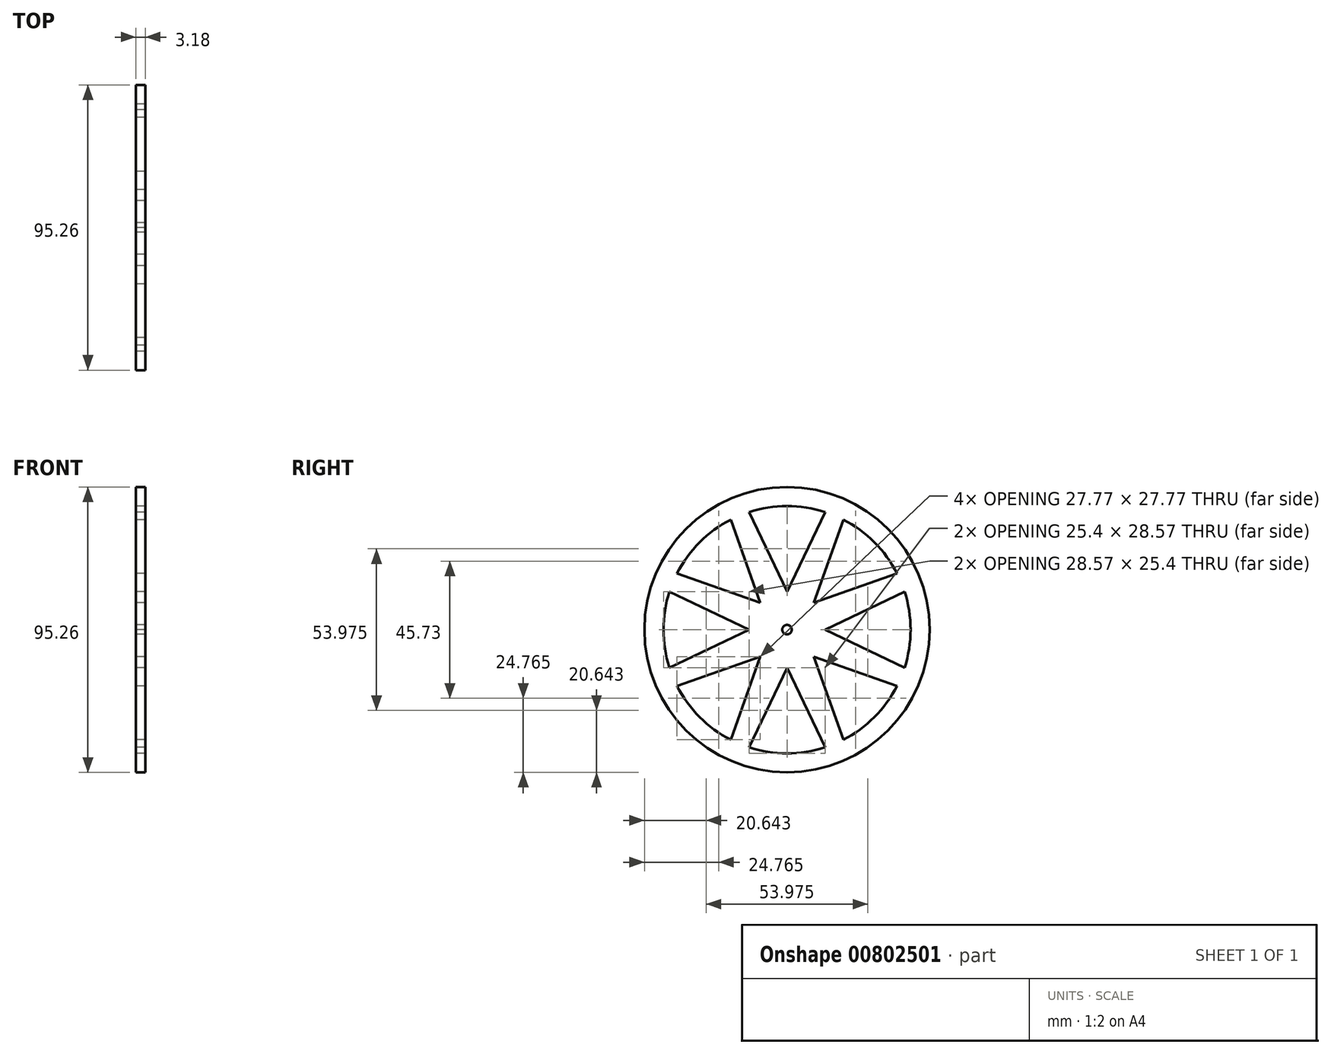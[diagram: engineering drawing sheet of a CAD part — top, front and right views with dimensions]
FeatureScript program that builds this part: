
annotation { "Feature Type Name" : "Feature", "Feature Type Description" : "" }
export const myFeature = defineFeature(function(context is Context, id is Id, definition is map)
    precondition{}
    {
        {
            var Q0;
            Q0=qCreatedBy(makeId("Right.planeOp"),FACE);
            var sketch = newSketch(context, id + "F0", { "sketchPlane" : qUnion([Q0])});
            skCircle(sketch, "E0", {"center": v(0, 0) * mm, "radius": 47.63 * mm});
            skCircle(sketch, "E1", {"center": v(0, 0) * mm, "radius": 41.28 * mm, "construction": true});
            skCircle(sketch, "E2", {"center": v(0, 0) * mm, "radius": 12.7 * mm, "construction": true});
            skArc(sketch, "E3", {"start": v(-12.7, 39.27) * mm, "mid": v(0, 41.28) * mm, "end": v(12.7, 39.27) * mm});
            skLineSegment(sketch, "E4", {"start": v(-12.7, 39.27) * mm, "end": v(0, 12.7) * mm});
            skLineSegment(sketch, "E5", {"start": v(0, 12.7) * mm, "end": v(12.7, 39.27) * mm});
            skLineSegment(sketch, "E6", {"start": v(-80.26, -80.26) * mm, "end": v(80.26, 80.26) * mm, "construction": true});
            skLineSegment(sketch, "E7", {"start": v(93.24, -93.24) * mm, "end": v(-93.24, 93.24) * mm, "construction": true});
            skLineSegment(sketch, "E8", {"start": v(18.79, 36.75) * mm, "end": v(8.98, 8.98) * mm});
            skLineSegment(sketch, "E9", {"start": v(36.75, 18.79) * mm, "end": v(8.98, 8.98) * mm});
            skArc(sketch, "E10", {"start": v(18.79, 36.75) * mm, "mid": v(29.19, 29.19) * mm, "end": v(36.75, 18.79) * mm});
            skArc(sketch, "E11", {"start": v(39.27, 12.7) * mm, "mid": v(41.28, 0) * mm, "end": v(39.27, -12.7) * mm});
            skLineSegment(sketch, "E12", {"start": v(39.27, 12.7) * mm, "end": v(12.7, 0) * mm});
            skLineSegment(sketch, "E13", {"start": v(12.7, 0) * mm, "end": v(39.27, -12.7) * mm});
            skArc(sketch, "E14", {"start": v(36.75, -18.79) * mm, "mid": v(29.19, -29.19) * mm, "end": v(18.79, -36.75) * mm});
            skLineSegment(sketch, "E15", {"start": v(36.75, -18.79) * mm, "end": v(8.98, -8.98) * mm});
            skLineSegment(sketch, "E16", {"start": v(8.98, -8.98) * mm, "end": v(18.79, -36.75) * mm});
            skArc(sketch, "E17", {"start": v(12.7, -39.27) * mm, "mid": v(0, -41.28) * mm, "end": v(-12.7, -39.27) * mm});
            skArc(sketch, "E18", {"start": v(-18.79, -36.75) * mm, "mid": v(-29.19, -29.19) * mm, "end": v(-36.75, -18.79) * mm});
            skArc(sketch, "E19", {"start": v(-39.27, -12.7) * mm, "mid": v(-41.28, 0) * mm, "end": v(-39.27, 12.7) * mm});
            skArc(sketch, "E20", {"start": v(-36.75, 18.79) * mm, "mid": v(-29.19, 29.19) * mm, "end": v(-18.79, 36.75) * mm});
            skLineSegment(sketch, "E21", {"start": v(12.7, -39.27) * mm, "end": v(0, -12.7) * mm});
            skLineSegment(sketch, "E22", {"start": v(0, -12.7) * mm, "end": v(-12.7, -39.27) * mm});
            skLineSegment(sketch, "E23", {"start": v(-18.79, -36.75) * mm, "end": v(-8.98, -8.98) * mm});
            skLineSegment(sketch, "E24", {"start": v(-8.98, -8.98) * mm, "end": v(-36.75, -18.79) * mm});
            skLineSegment(sketch, "E25", {"start": v(-39.27, -12.7) * mm, "end": v(-12.7, 0) * mm});
            skLineSegment(sketch, "E26", {"start": v(-12.7, 0) * mm, "end": v(-39.27, 12.7) * mm});
            skLineSegment(sketch, "E27", {"start": v(-36.75, 18.79) * mm, "end": v(-8.98, 8.98) * mm});
            skLineSegment(sketch, "E28", {"start": v(-8.98, 8.98) * mm, "end": v(-18.79, 36.75) * mm});
            skCircle(sketch, "E29", {"center": v(0, 0) * mm, "radius": 1.59 * mm});
            skSolve(sketch);
        }
        {
            var Q0;
            Q0=qSketchRegion(id+"F0",true);
            extrude(context, id + "F1", {"entities" : qUnion([Q0]), "depth" : 3.17 * mm, "offsetDistance" : 25.4 * mm});
        }
    });
